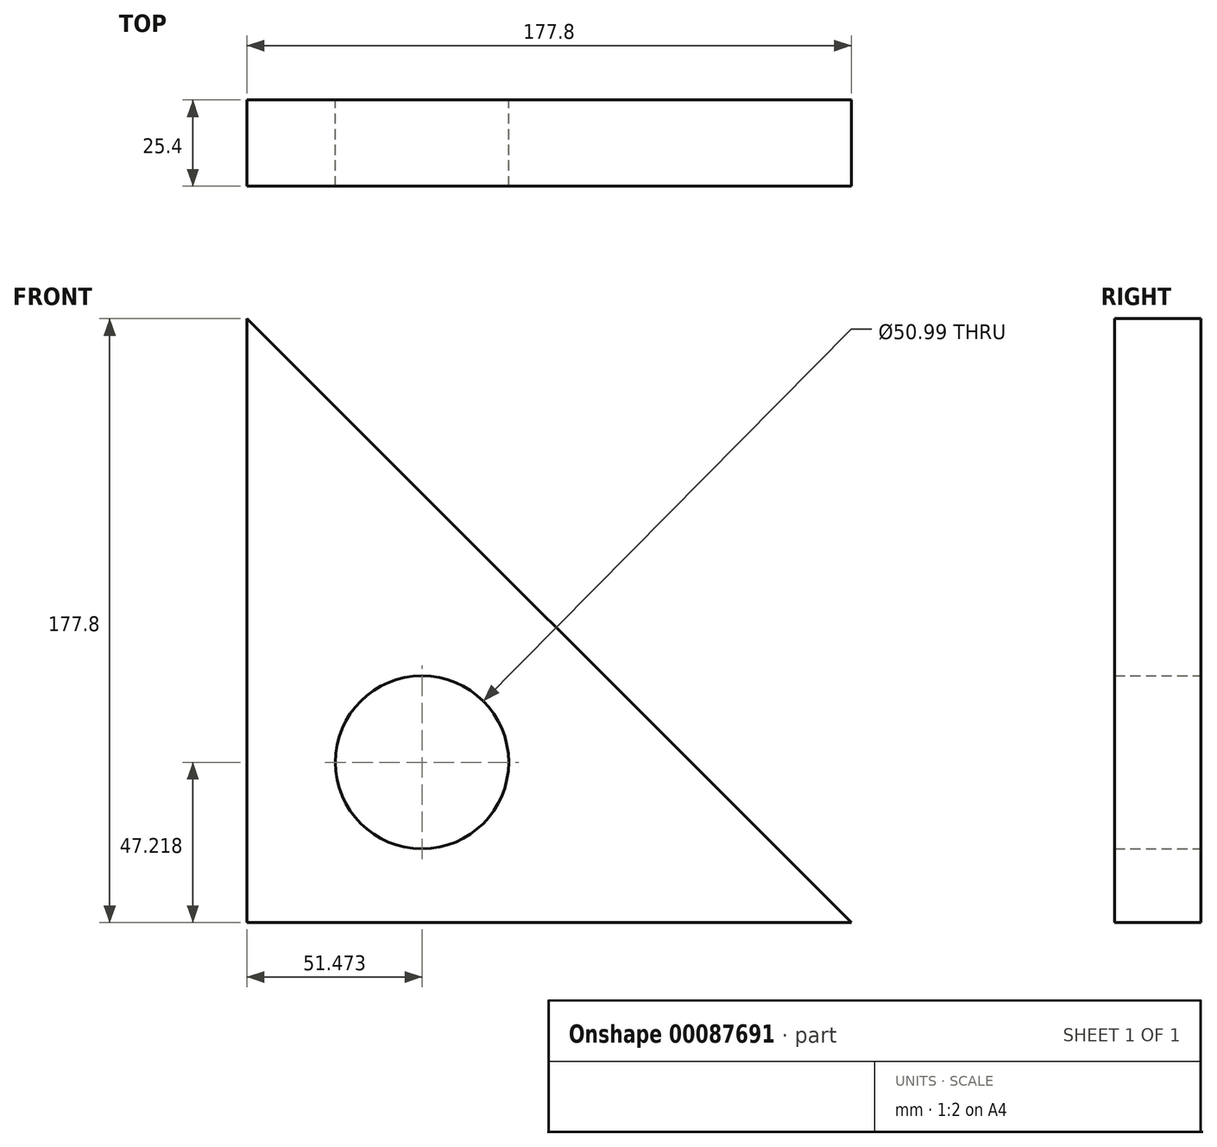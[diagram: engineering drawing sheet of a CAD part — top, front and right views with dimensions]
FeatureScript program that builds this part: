
annotation { "Feature Type Name" : "Feature", "Feature Type Description" : "" }
export const myFeature = defineFeature(function(context is Context, id is Id, definition is map)
    precondition{}
    {
        {
            var Q0;
            Q0=qCreatedBy(makeId("Front.planeOp"),FACE);
            var sketch = newSketch(context, id + "F0", { "sketchPlane" : qUnion([Q0])});
            skLineSegment(sketch, "E0", {"start": v(0, 0) * mm, "end": v(0, 177.8) * mm});
            skLineSegment(sketch, "E1", {"start": v(0, 177.8) * mm, "end": v(177.8, 0) * mm});
            skLineSegment(sketch, "E2", {"start": v(177.8, 0) * mm, "end": v(0, 0) * mm});
            skCircle(sketch, "E3", {"center": v(51.47, 47.22) * mm, "radius": 25.5 * mm});
            skLineSegment(sketch, "E4", {"start": v(0, 0) * mm, "end": v(92.73, 85.07) * mm});
            skSolve(sketch);
        }
        {
            var Q0;
            Q0 = qSketchRegion(id + "F0", true);
            extrude(context, id + "F1", {"entities" : qUnion([Q0]), "depth" : 25.4 * mm});
        }
    });
